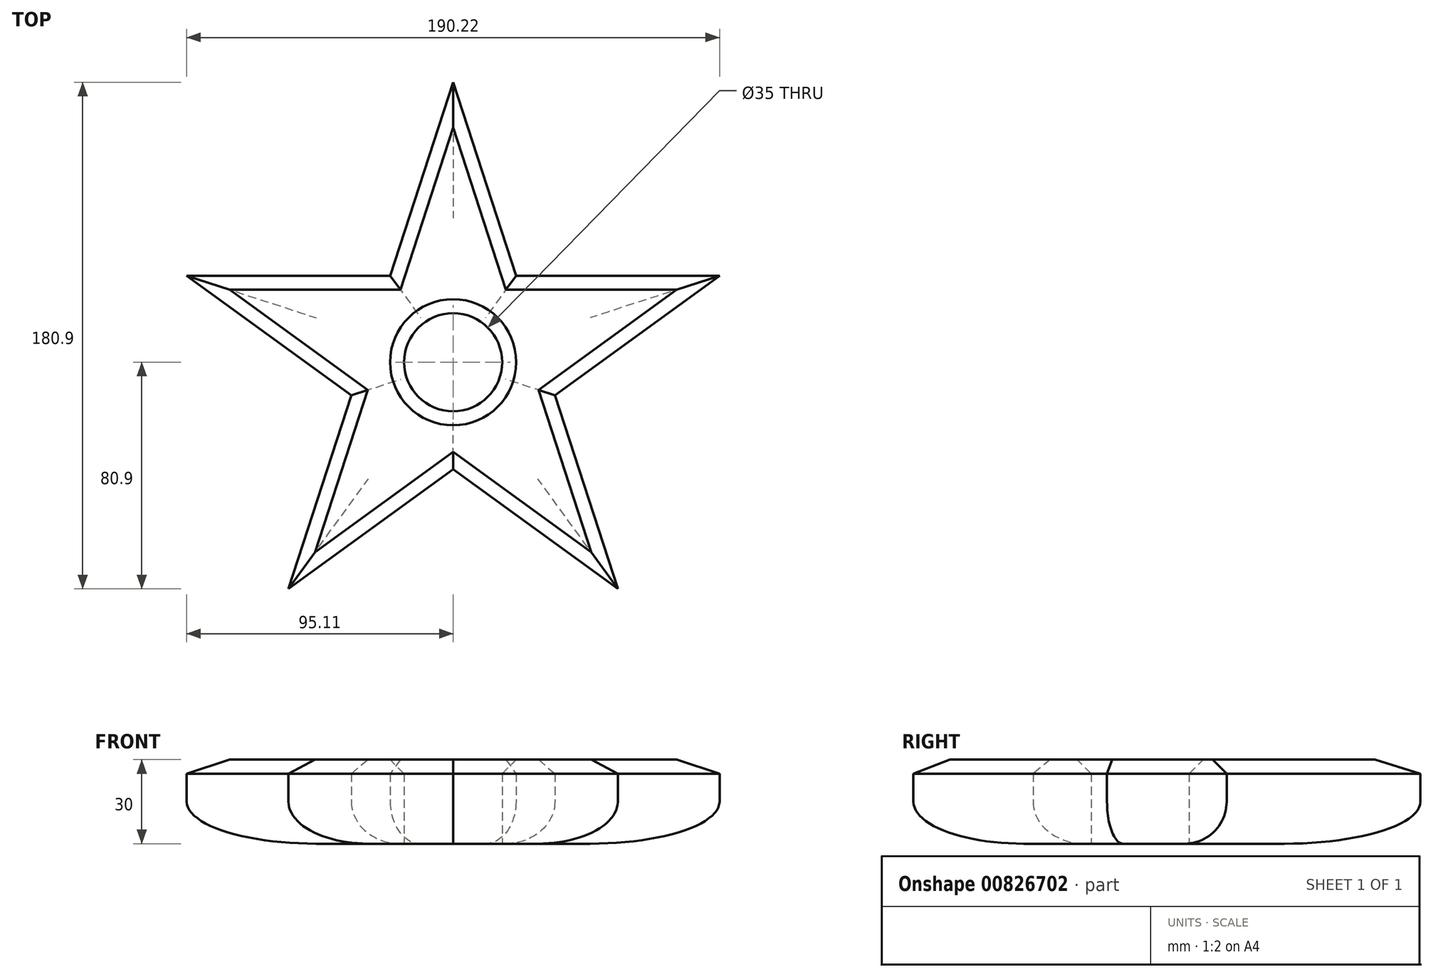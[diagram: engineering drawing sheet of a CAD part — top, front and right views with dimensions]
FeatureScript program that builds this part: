
annotation { "Feature Type Name" : "Feature", "Feature Type Description" : "" }
export const myFeature = defineFeature(function(context is Context, id is Id, definition is map)
    precondition{}
    {
        {
            var Q0;
            Q0=qCreatedBy(makeId("Top.planeOp"),FACE);
            var sketch = newSketch(context, id + "F0", { "sketchPlane" : qUnion([Q0])});
            skCircle(sketch, "E0.cCircle", {"center": v(0, 0) * mm, "radius": 100 * mm, "construction": true});
            skLineSegment(sketch, "E0.0", {"start": v(0, 100) * mm, "end": v(95.1, 30.9) * mm});
            skLineSegment(sketch, "E0.1", {"start": v(95.1, 30.9) * mm, "end": v(58.78, -80.9) * mm});
            skLineSegment(sketch, "E0.2", {"start": v(58.78, -80.9) * mm, "end": v(-58.78, -80.9) * mm});
            skLineSegment(sketch, "E0.3", {"start": v(-58.78, -80.9) * mm, "end": v(-95.1, 30.9) * mm});
            skLineSegment(sketch, "E0.4", {"start": v(-95.1, 30.9) * mm, "end": v(0, 100) * mm});
            skLineSegment(sketch, "E1", {"start": v(0, 100) * mm, "end": v(-22.45, 30.9) * mm});
            skLineSegment(sketch, "E2", {"start": v(58.78, -80.9) * mm, "end": v(36.33, -11.8) * mm});
            skLineSegment(sketch, "E3", {"start": v(-95.1, 30.9) * mm, "end": v(-22.45, 30.9) * mm});
            skLineSegment(sketch, "E4", {"start": v(95.1, 30.9) * mm, "end": v(36.33, -11.8) * mm});
            skLineSegment(sketch, "E5", {"start": v(-95.1, 30.9) * mm, "end": v(-36.33, -11.8) * mm});
            skLineSegment(sketch, "E6.trimOffspring", {"start": v(22.45, 30.9) * mm, "end": v(95.1, 30.9) * mm});
            skLineSegment(sketch, "E7.trimOffspring", {"start": v(0, -38.2) * mm, "end": v(58.78, -80.9) * mm});
            skLineSegment(sketch, "E8.trimOffspring", {"start": v(0, -38.2) * mm, "end": v(-58.78, -80.9) * mm});
            skLineSegment(sketch, "E9.trimOffspring", {"start": v(22.45, 30.9) * mm, "end": v(0, 100) * mm});
            skLineSegment(sketch, "E10.trimOffspring", {"start": v(-36.33, -11.8) * mm, "end": v(-58.78, -80.9) * mm});
            skSolve(sketch);
        }
        {
            var Q0;
            Q0=makeQuery(id+"F0.imprint","IMPRINT",FACE,{"disambiguationData":[TD([[makeQuery(id+"F0.imprint","IMPRINT",EDGE,{"derivedFrom":sQuery(id+"F0.wireOp",EDGE,"E1")}),1.0]])]});
            extrude(context, id + "F1", {"entities" : qUnion([Q0]), "depth" : 30 * mm, "offsetDistance" : 25 * mm});
        }
        {
            var Q0;
            Q0=makeQuery(id+"F1.opExtrude","CAP_FACE",FACE,{"disambiguationData":[OSD([sQuery(id+"F0.wireOp",EDGE,"E1"),sQuery(id+"F0.wireOp",EDGE,"E2"),sQuery(id+"F0.wireOp",EDGE,"E3"),sQuery(id+"F0.wireOp",EDGE,"E4"),sQuery(id+"F0.wireOp",EDGE,"E5"),sQuery(id+"F0.wireOp",EDGE,"E6.trimOffspring"),sQuery(id+"F0.wireOp",EDGE,"E7.trimOffspring"),sQuery(id+"F0.wireOp",EDGE,"E8.trimOffspring"),sQuery(id+"F0.wireOp",EDGE,"E9.trimOffspring"),sQuery(id+"F0.wireOp",EDGE,"E10.trimOffspring")])],"isStart":false});
            chamfer(context, id + "F2", {"entities" : qUnion([Q0]), "width" : 5 * mm, "tangentPropagation" : true});
        }
        {
            var Q0;
            Q0=makeQuery(id+"F1.opExtrude","CAP_FACE",FACE,{"disambiguationData":[OSD([sQuery(id+"F0.wireOp",EDGE,"E1"),sQuery(id+"F0.wireOp",EDGE,"E2"),sQuery(id+"F0.wireOp",EDGE,"E3"),sQuery(id+"F0.wireOp",EDGE,"E4"),sQuery(id+"F0.wireOp",EDGE,"E5"),sQuery(id+"F0.wireOp",EDGE,"E6.trimOffspring"),sQuery(id+"F0.wireOp",EDGE,"E7.trimOffspring"),sQuery(id+"F0.wireOp",EDGE,"E8.trimOffspring"),sQuery(id+"F0.wireOp",EDGE,"E9.trimOffspring"),sQuery(id+"F0.wireOp",EDGE,"E10.trimOffspring")])],"isStart":true});
            fillet(context, id + "F3", {"entities" : qUnion([Q0]), "radius" : 15 * mm, "tangentPropagation" : true, "allowEdgeOverflow" : false});
        }
        {
            var Q0;
            Q0=makeQuery(id+"F1.opExtrude","CAP_FACE",FACE,{"disambiguationData":[OSD([sQuery(id+"F0.wireOp",EDGE,"E1"),sQuery(id+"F0.wireOp",EDGE,"E2"),sQuery(id+"F0.wireOp",EDGE,"E3"),sQuery(id+"F0.wireOp",EDGE,"E4"),sQuery(id+"F0.wireOp",EDGE,"E5"),sQuery(id+"F0.wireOp",EDGE,"E6.trimOffspring"),sQuery(id+"F0.wireOp",EDGE,"E7.trimOffspring"),sQuery(id+"F0.wireOp",EDGE,"E8.trimOffspring"),sQuery(id+"F0.wireOp",EDGE,"E9.trimOffspring"),sQuery(id+"F0.wireOp",EDGE,"E10.trimOffspring")])],"isStart":true});
            var sketch = newSketch(context, id + "F4", { "sketchPlane" : qUnion([Q0])});
            skCircle(sketch, "E11", {"center": v(0, 0) * mm, "radius": 17.5 * mm});
            skSolve(sketch);
        }
        {
            var Q0;
            Q0=makeQuery(id+"F4.imprint","IMPRINT",FACE,{"disambiguationData":[TD([[makeQuery(id+"F4.imprint","IMPRINT",EDGE,{"derivedFrom":sQuery(id+"F4.wireOp",EDGE,"E11")}),1.0]])]});
            extrude(context, id + "F5", {"entities" : qUnion([Q0]), "operationType" : NewBodyOperationType.REMOVE, "oppositeDirection" : true, "depth" : 40 * mm, "offsetDistance" : 25 * mm});
        }
        {
            var Q0;
            Q0=makeQuery(id+"F5.boolean.opBoolean","INTERSECT",EDGE,{"derivedFrom":[makeQuery(id+"F1.opExtrude","CAP_FACE",FACE,{"disambiguationData":[OSD([sQuery(id+"F0.wireOp",EDGE,"E1"),sQuery(id+"F0.wireOp",EDGE,"E2"),sQuery(id+"F0.wireOp",EDGE,"E3"),sQuery(id+"F0.wireOp",EDGE,"E4"),sQuery(id+"F0.wireOp",EDGE,"E5"),sQuery(id+"F0.wireOp",EDGE,"E6.trimOffspring"),sQuery(id+"F0.wireOp",EDGE,"E7.trimOffspring"),sQuery(id+"F0.wireOp",EDGE,"E8.trimOffspring"),sQuery(id+"F0.wireOp",EDGE,"E9.trimOffspring"),sQuery(id+"F0.wireOp",EDGE,"E10.trimOffspring")])],"isStart":false}),makeQuery(id+"F5.opExtrude","SWEPT_FACE",FACE,{"disambiguationData":[OSD([sQuery(id+"F4.wireOp",EDGE,"E11")])]})]});
            chamfer(context, id + "F6", {"entities" : qUnion([Q0]), "width" : 5 * mm, "tangentPropagation" : true});
        }
    });
